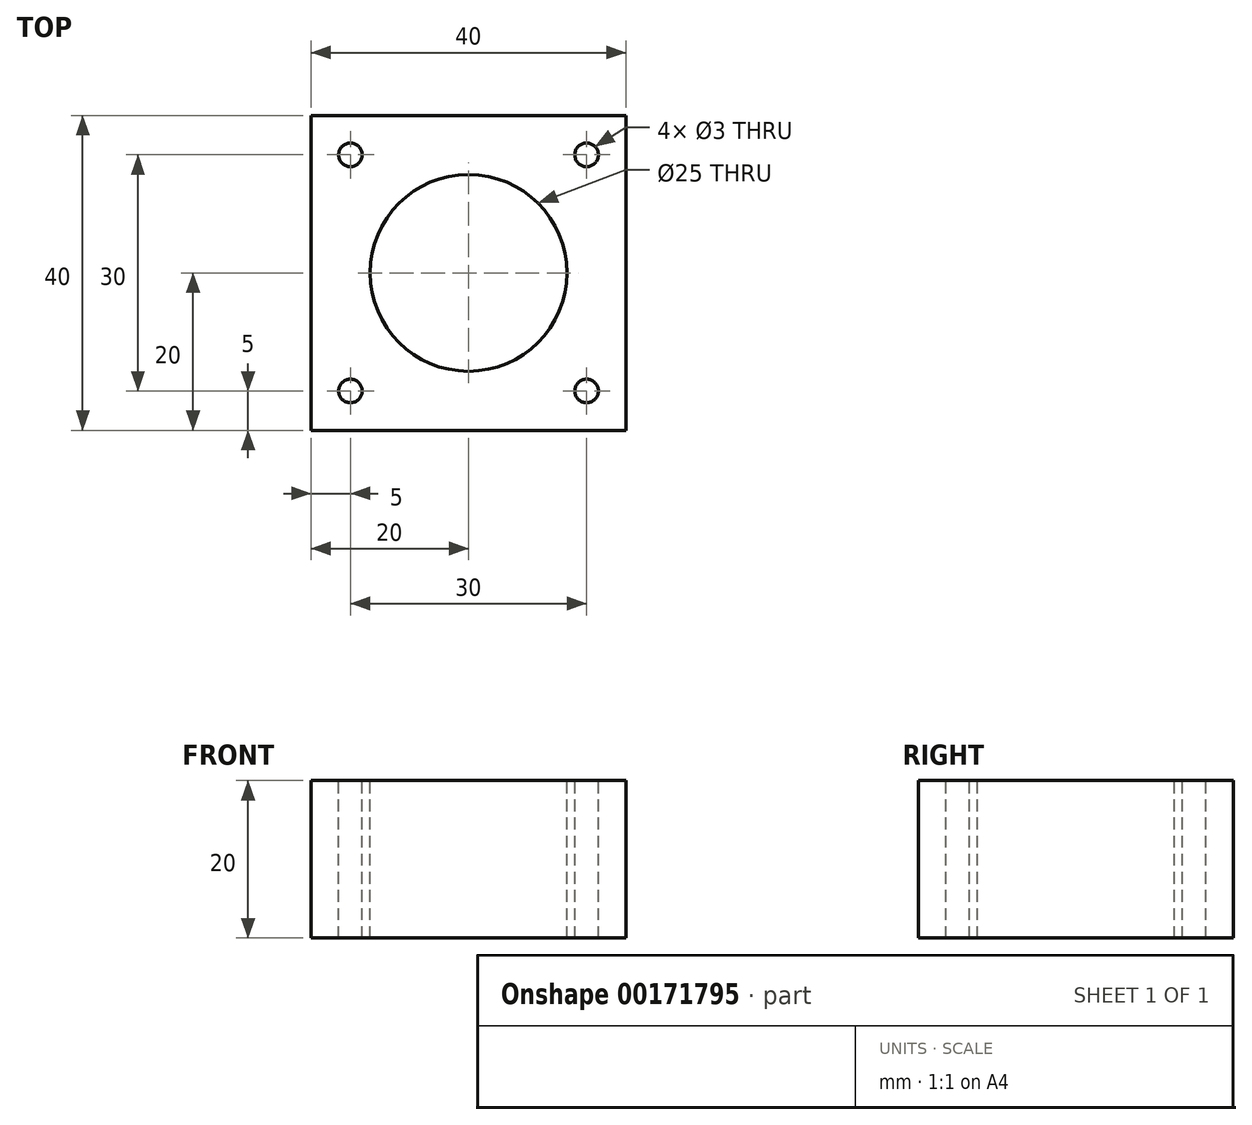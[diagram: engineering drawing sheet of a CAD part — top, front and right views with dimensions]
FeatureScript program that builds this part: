
annotation { "Feature Type Name" : "Feature", "Feature Type Description" : "" }
export const myFeature = defineFeature(function(context is Context, id is Id, definition is map)
    precondition{}
    {
        {
            var Q0;
            Q0=qCreatedBy(makeId("Top.planeOp"),FACE);
            var sketch = newSketch(context, id + "F0", { "sketchPlane" : qUnion([Q0])});
            skLineSegment(sketch, "E0.bottom", {"start": v(-20, 20) * mm, "end": v(20, 20) * mm});
            skLineSegment(sketch, "E0.top", {"start": v(-20, -20) * mm, "end": v(20, -20) * mm});
            skLineSegment(sketch, "E0.left", {"start": v(-20, 20) * mm, "end": v(-20, -20) * mm});
            skLineSegment(sketch, "E0.right", {"start": v(20, 20) * mm, "end": v(20, -20) * mm});
            skPoint(sketch, "E0.middle", {"position": v(0, 0) * mm});
            skSolve(sketch);
        }
        {
            var Q0;
            Q0 = qSketchRegion(id + "F0", true);
            extrude(context, id + "F1", {"entities" : qUnion([Q0]), "depth" : 20 * mm});
        }
        {
            var Q0;
            Q0=makeQuery(id+"F1.opExtrude","CAP_FACE",FACE,{"disambiguationData":[OSD([sQuery(id+"F0.wireOp",EDGE,"E0.bottom"),sQuery(id+"F0.wireOp",EDGE,"E0.top"),sQuery(id+"F0.wireOp",EDGE,"E0.left"),sQuery(id+"F0.wireOp",EDGE,"E0.right")])],"isStart":false});
            var sketch = newSketch(context, id + "F2", { "sketchPlane" : qUnion([Q0])});
            skCircle(sketch, "E1", {"center": v(0, 0) * mm, "radius": 12.5 * mm});
            skSolve(sketch);
        }
        {
            var Q0;
            Q0=makeQuery(id+"F2.imprint","IMPRINT",FACE,{"disambiguationData":[TD([[makeQuery(id+"F2.imprint","IMPRINT",EDGE,{"derivedFrom":sQuery(id+"F2.wireOp",EDGE,"E1")}),1.0]])]});
            extrude(context, id + "F3", {"entities" : qUnion([Q0]), "operationType" : NewBodyOperationType.REMOVE, "endBound" : BoundingType.UP_TO_NEXT, "oppositeDirection" : true, "depth" : 25.4 * mm});
        }
        {
            var Q0;
            Q0=makeQuery(id+"F1.opExtrude","CAP_FACE",FACE,{"disambiguationData":[OSD([sQuery(id+"F0.wireOp",EDGE,"E0.bottom"),sQuery(id+"F0.wireOp",EDGE,"E0.top"),sQuery(id+"F0.wireOp",EDGE,"E0.left"),sQuery(id+"F0.wireOp",EDGE,"E0.right")])],"isStart":false});
            var sketch = newSketch(context, id + "F4", { "sketchPlane" : qUnion([Q0])});
            skCircle(sketch, "E2", {"center": v(15, 15) * mm, "radius": 1.5 * mm});
            skCircle(sketch, "E3", {"center": v(15, -15) * mm, "radius": 1.5 * mm});
            skCircle(sketch, "E4", {"center": v(-15, -15) * mm, "radius": 1.5 * mm});
            skCircle(sketch, "E5", {"center": v(-15, 15) * mm, "radius": 1.5 * mm});
            skSolve(sketch);
        }
        {
            var Q0;
            Q0=makeQuery(id+"F4.imprint","IMPRINT",FACE,{"disambiguationData":[TD([[makeQuery(id+"F4.imprint","IMPRINT",EDGE,{"derivedFrom":sQuery(id+"F4.wireOp",EDGE,"E2")}),1.0]])]});
            var Q1;
            Q1=makeQuery(id+"F4.imprint","IMPRINT",FACE,{"disambiguationData":[TD([[makeQuery(id+"F4.imprint","IMPRINT",EDGE,{"derivedFrom":sQuery(id+"F4.wireOp",EDGE,"E3")}),1.0]])]});
            var Q2;
            Q2=makeQuery(id+"F4.imprint","IMPRINT",FACE,{"disambiguationData":[TD([[makeQuery(id+"F4.imprint","IMPRINT",EDGE,{"derivedFrom":sQuery(id+"F4.wireOp",EDGE,"E4")}),1.0]])]});
            var Q3;
            Q3=makeQuery(id+"F4.imprint","IMPRINT",FACE,{"disambiguationData":[TD([[makeQuery(id+"F4.imprint","IMPRINT",EDGE,{"derivedFrom":sQuery(id+"F4.wireOp",EDGE,"E5")}),1.0]])]});
            extrude(context, id + "F5", {"entities" : qUnion([Q0, Q1, Q2, Q3]), "operationType" : NewBodyOperationType.REMOVE, "oppositeDirection" : true, "depth" : 25.4 * mm});
        }
    });
